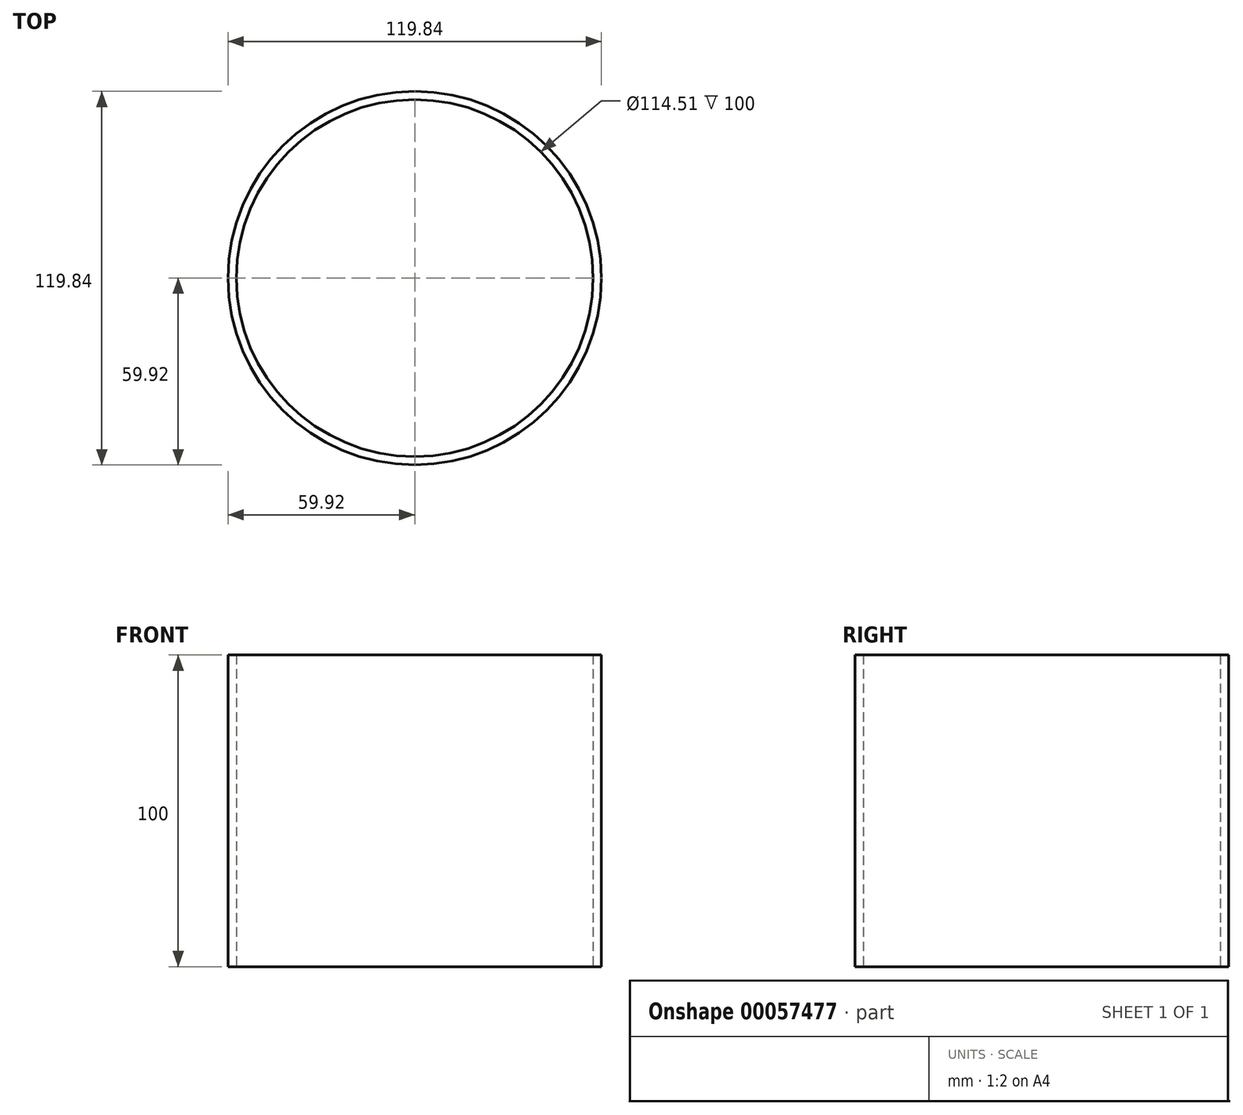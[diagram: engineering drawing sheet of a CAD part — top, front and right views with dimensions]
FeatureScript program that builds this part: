
annotation { "Feature Type Name" : "Feature", "Feature Type Description" : "" }
export const myFeature = defineFeature(function(context is Context, id is Id, definition is map)
    precondition{}
    {
        {
            var Q0;
            Q0=qCreatedBy(makeId("Top.planeOp"),FACE);
            var sketch = newSketch(context, id + "F0", { "sketchPlane" : qUnion([Q0])});
            skCircle(sketch, "E0", {"center": v(0, 0) * mm, "radius": 59.92 * mm});
            skCircle(sketch, "E1", {"center": v(0, 0) * mm, "radius": 57.26 * mm});
            skSolve(sketch);
        }
        {
            var Q0;
            Q0=makeQuery(id+"F0.imprint","IMPRINT",FACE,{"disambiguationData":[TD([[makeQuery(id+"F0.imprint","IMPRINT",EDGE,{"derivedFrom":sQuery(id+"F0.wireOp",EDGE,"E0")}),1.0]])]});
            extrude(context, id + "F1", {"entities" : qUnion([Q0]), "depth" : 100 * mm});
        }
    });
